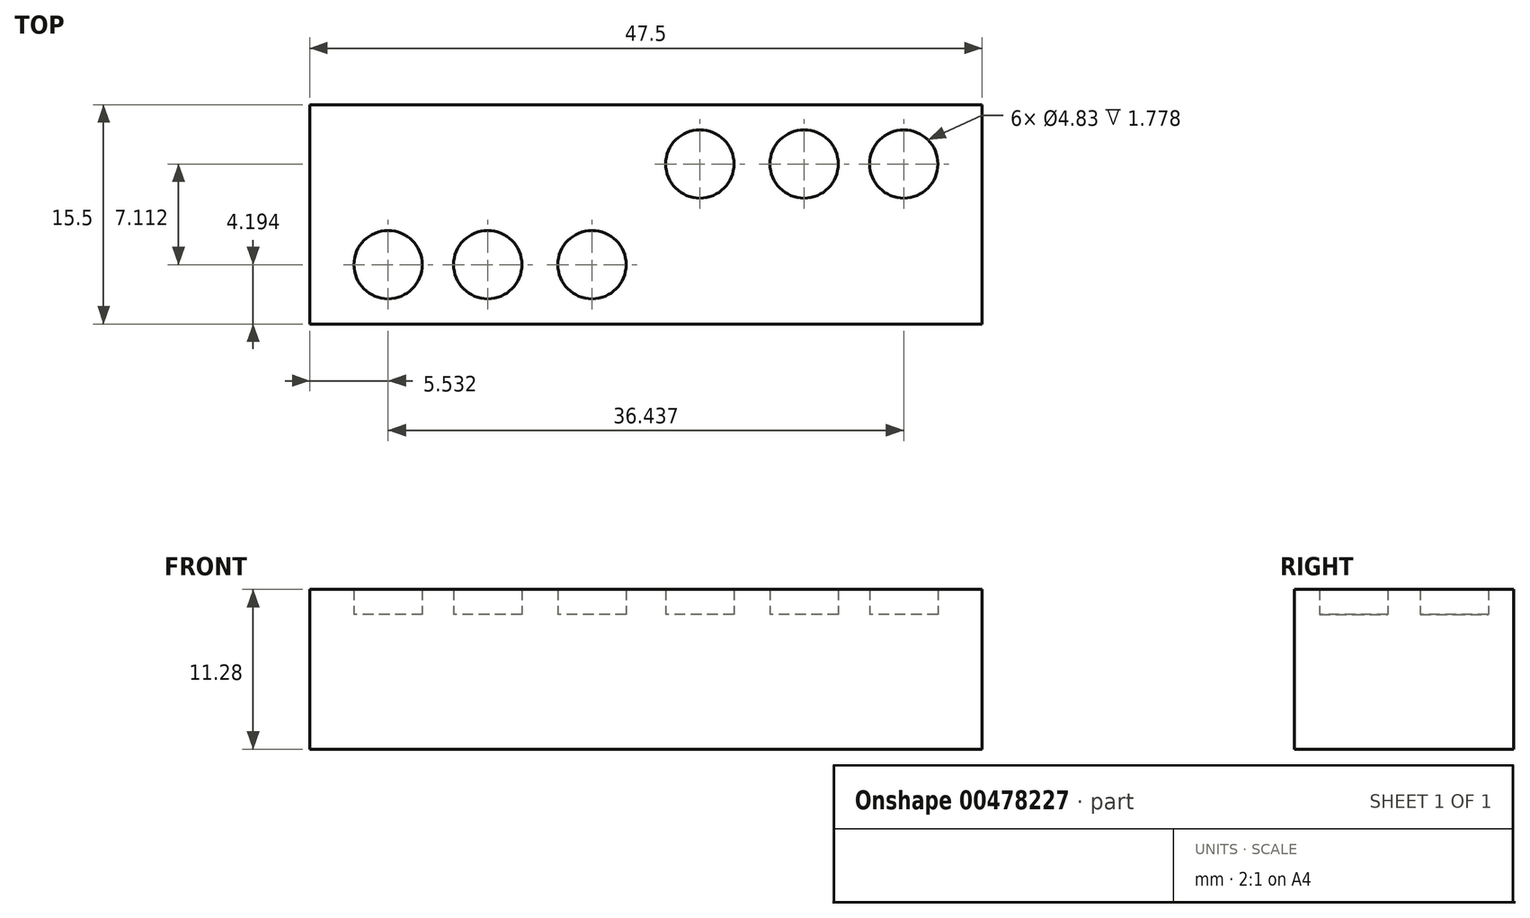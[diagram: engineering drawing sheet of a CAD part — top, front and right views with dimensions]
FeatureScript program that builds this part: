
annotation { "Feature Type Name" : "Feature", "Feature Type Description" : "" }
export const myFeature = defineFeature(function(context is Context, id is Id, definition is map)
    precondition{}
    {
        {
            var Q0;
            Q0=qCreatedBy(makeId("Top.planeOp"),FACE);
            var sketch = newSketch(context, id + "F0", { "sketchPlane" : qUnion([Q0])});
            skLineSegment(sketch, "E0.bottom", {"start": v(-23.75, 7.75) * mm, "end": v(23.75, 7.75) * mm});
            skLineSegment(sketch, "E0.top", {"start": v(-23.75, -7.75) * mm, "end": v(23.75, -7.75) * mm});
            skLineSegment(sketch, "E0.left", {"start": v(-23.75, 7.75) * mm, "end": v(-23.75, -7.75) * mm});
            skLineSegment(sketch, "E0.right", {"start": v(23.75, 7.75) * mm, "end": v(23.75, -7.75) * mm});
            skPoint(sketch, "E0.middle", {"position": v(0, 0) * mm});
            skSolve(sketch);
        }
        {
            var Q0;
            Q0=makeQuery(id+"F0.imprint","IMPRINT",FACE,{"disambiguationData":[TD([[makeQuery(id+"F0.imprint","IMPRINT",EDGE,{"derivedFrom":sQuery(id+"F0.wireOp",EDGE,"E0.bottom")}),-1.0]])]});
            extrude(context, id + "F1", {"entities" : qUnion([Q0]), "depth" : 9.5 * mm});
        }
        {
            var Q0;
            Q0=makeQuery(id+"F1.opExtrude","CAP_FACE",FACE,{"disambiguationData":[OSD([sQuery(id+"F0.wireOp",EDGE,"E0.bottom"),sQuery(id+"F0.wireOp",EDGE,"E0.top"),sQuery(id+"F0.wireOp",EDGE,"E0.left"),sQuery(id+"F0.wireOp",EDGE,"E0.right")])],"isStart":false});
            var sketch = newSketch(context, id + "F2", { "sketchPlane" : qUnion([Q0])});
            skCircle(sketch, "E1", {"center": v(-18.22, 3.56) * mm, "radius": 2.41 * mm});
            skCircle(sketch, "E2", {"center": v(-11.18, 3.56) * mm, "radius": 2.41 * mm});
            skCircle(sketch, "E3", {"center": v(-3.81, 3.56) * mm, "radius": 2.41 * mm});
            skCircle(sketch, "E4.MirrorC", {"center": v(3.81, 3.56) * mm, "radius": 2.41 * mm});
            skCircle(sketch, "E5.MirrorC", {"center": v(11.18, 3.56) * mm, "radius": 2.41 * mm});
            skCircle(sketch, "E6.MirrorC", {"center": v(18.22, 3.56) * mm, "radius": 2.41 * mm});
            skCircle(sketch, "E7.MirrorC", {"center": v(18.22, -3.56) * mm, "radius": 2.41 * mm});
            skCircle(sketch, "E8.MirrorC", {"center": v(11.18, -3.56) * mm, "radius": 2.41 * mm});
            skCircle(sketch, "E9.MirrorC", {"center": v(3.81, -3.56) * mm, "radius": 2.41 * mm});
            skCircle(sketch, "E10.MirrorC", {"center": v(-3.81, -3.56) * mm, "radius": 2.41 * mm});
            skCircle(sketch, "E11.MirrorC", {"center": v(-11.18, -3.56) * mm, "radius": 2.41 * mm});
            skCircle(sketch, "E12.MirrorC", {"center": v(-18.22, -3.56) * mm, "radius": 2.41 * mm});
            skSolve(sketch);
        }
        {
            var Q0;
            Q0=makeQuery(id+"F2.imprint","IMPRINT",FACE,{"disambiguationData":[TD([[makeQuery(id+"F2.imprint","IMPRINT",EDGE,{"derivedFrom":sQuery(id+"F2.wireOp",EDGE,"E1")}),1.0]])]});
            var Q1;
            Q1=makeQuery(id+"F2.imprint","IMPRINT",FACE,{"disambiguationData":[TD([[makeQuery(id+"F2.imprint","IMPRINT",EDGE,{"derivedFrom":sQuery(id+"F2.wireOp",EDGE,"E2")}),1.0]])]});
            var Q2;
            Q2=makeQuery(id+"F2.imprint","IMPRINT",FACE,{"disambiguationData":[TD([[makeQuery(id+"F2.imprint","IMPRINT",EDGE,{"derivedFrom":sQuery(id+"F2.wireOp",EDGE,"E3")}),1.0]])]});
            var Q3;
            Q3=makeQuery(id+"F2.imprint","IMPRINT",FACE,{"disambiguationData":[TD([[makeQuery(id+"F2.imprint","IMPRINT",EDGE,{"derivedFrom":sQuery(id+"F2.wireOp",EDGE,"E4.MirrorC")}),-1.0]])]});
            var Q4;
            Q4=makeQuery(id+"F2.imprint","IMPRINT",FACE,{"disambiguationData":[TD([[makeQuery(id+"F2.imprint","IMPRINT",EDGE,{"derivedFrom":sQuery(id+"F2.wireOp",EDGE,"E5.MirrorC")}),-1.0]])]});
            var Q5;
            Q5=makeQuery(id+"F2.imprint","IMPRINT",FACE,{"disambiguationData":[TD([[makeQuery(id+"F2.imprint","IMPRINT",EDGE,{"derivedFrom":sQuery(id+"F2.wireOp",EDGE,"E6.MirrorC")}),-1.0]])]});
            var Q6;
            Q6=makeQuery(id+"F2.imprint","IMPRINT",FACE,{"disambiguationData":[TD([[makeQuery(id+"F2.imprint","IMPRINT",EDGE,{"derivedFrom":sQuery(id+"F2.wireOp",EDGE,"E7.MirrorC")}),1.0]])]});
            var Q7;
            Q7=makeQuery(id+"F2.imprint","IMPRINT",FACE,{"disambiguationData":[TD([[makeQuery(id+"F2.imprint","IMPRINT",EDGE,{"derivedFrom":sQuery(id+"F2.wireOp",EDGE,"E8.MirrorC")}),1.0]])]});
            var Q8;
            Q8=makeQuery(id+"F2.imprint","IMPRINT",FACE,{"disambiguationData":[TD([[makeQuery(id+"F2.imprint","IMPRINT",EDGE,{"derivedFrom":sQuery(id+"F2.wireOp",EDGE,"E11.MirrorC")}),-1.0]])]});
            var Q9;
            Q9=makeQuery(id+"F2.imprint","IMPRINT",FACE,{"disambiguationData":[TD([[makeQuery(id+"F2.imprint","IMPRINT",EDGE,{"derivedFrom":sQuery(id+"F2.wireOp",EDGE,"E10.MirrorC")}),-1.0]])]});
            var Q10;
            Q10=makeQuery(id+"F2.imprint","IMPRINT",FACE,{"disambiguationData":[TD([[makeQuery(id+"F2.imprint","IMPRINT",EDGE,{"derivedFrom":sQuery(id+"F2.wireOp",EDGE,"E9.MirrorC")}),1.0]])]});
            var Q11;
            Q11=makeQuery(id+"F2.imprint","IMPRINT",FACE,{"disambiguationData":[TD([[makeQuery(id+"F2.imprint","IMPRINT",EDGE,{"derivedFrom":sQuery(id+"F2.wireOp",EDGE,"E12.MirrorC")}),-1.0]])]});
            extrude(context, id + "F3", {"entities" : qUnion([Q0, Q1, Q2, Q3, Q4, Q5, Q6, Q7, Q8, Q9, Q10, Q11]), "operationType" : NewBodyOperationType.ADD, "depth" : 1.78 * mm, "offsetDistance" : 25.4 * mm});
        }
    });
